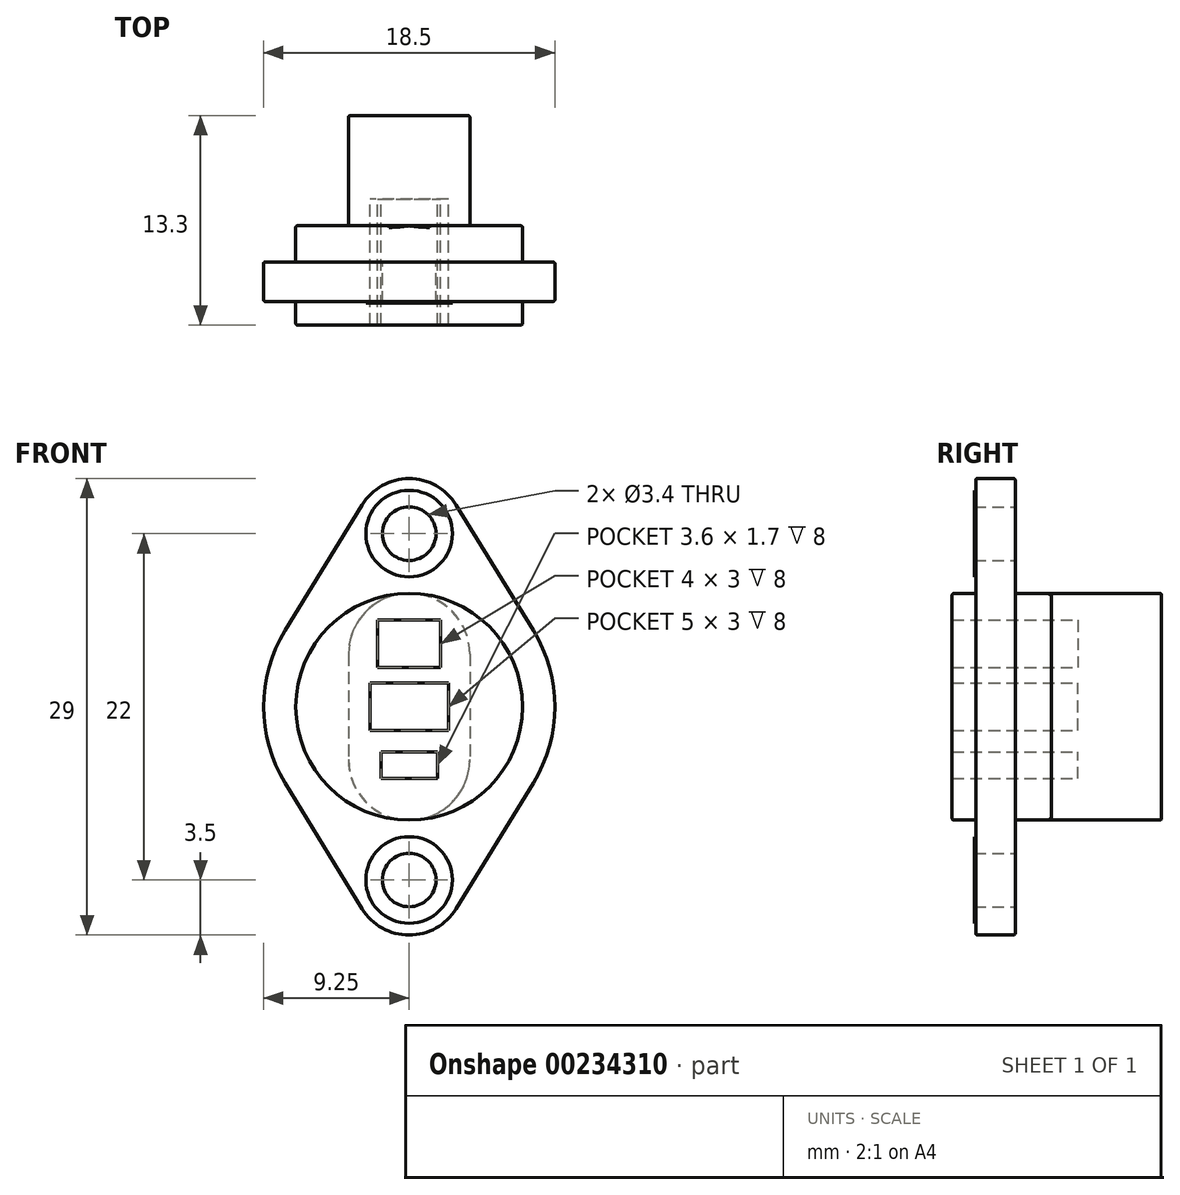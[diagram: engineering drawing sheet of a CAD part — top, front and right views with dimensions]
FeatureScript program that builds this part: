
annotation { "Feature Type Name" : "Feature", "Feature Type Description" : "" }
export const myFeature = defineFeature(function(context is Context, id is Id, definition is map)
    precondition{}
    {
        {
            var Q0;
            Q0=qCreatedBy(makeId("Front.planeOp"),FACE);
            var sketch = newSketch(context, id + "F0", { "sketchPlane" : qUnion([Q0])});
            skCircle(sketch, "E0", {"center": v(0, 11) * mm, "radius": 1.7 * mm});
            skCircle(sketch, "E1", {"center": v(0, -11) * mm, "radius": 1.7 * mm});
            skLineSegment(sketch, "E2", {"start": v(0, 11) * mm, "end": v(0, -11) * mm, "construction": true});
            skPoint(sketch, "E3", {"position": v(0, 0) * mm});
            skCircle(sketch, "E4", {"center": v(0, 0) * mm, "radius": 7.2 * mm});
            skCircle(sketch, "E5", {"center": v(0, -11) * mm, "radius": 2.75 * mm});
            skCircle(sketch, "E6", {"center": v(0, 11) * mm, "radius": 2.75 * mm});
            skCircle(sketch, "E7", {"center": v(0, 11) * mm, "radius": 3.5 * mm});
            skCircle(sketch, "E8", {"center": v(0, -11) * mm, "radius": 3.5 * mm});
            skCircle(sketch, "E9", {"center": v(0, 0) * mm, "radius": 9.25 * mm});
            skLineSegment(sketch, "E10", {"start": v(-2.98, 12.83) * mm, "end": v(-7.89, 4.84) * mm});
            skLineSegment(sketch, "E11", {"start": v(2.98, 12.83) * mm, "end": v(7.89, 4.84) * mm});
            skLineSegment(sketch, "E12", {"start": v(-2.98, -12.83) * mm, "end": v(-7.89, -4.84) * mm});
            skLineSegment(sketch, "E13.bottom", {"start": v(2.5, -1.5) * mm, "end": v(-2.5, -1.5) * mm});
            skLineSegment(sketch, "E13.top", {"start": v(2.5, 1.5) * mm, "end": v(-2.5, 1.5) * mm});
            skLineSegment(sketch, "E13.left", {"start": v(2.5, -1.5) * mm, "end": v(2.5, 1.5) * mm});
            skLineSegment(sketch, "E13.right", {"start": v(-2.5, -1.5) * mm, "end": v(-2.5, 1.5) * mm});
            skLineSegment(sketch, "E14.bottom", {"start": v(-2, 5.5) * mm, "end": v(2, 5.5) * mm});
            skLineSegment(sketch, "E14.top", {"start": v(-2, 2.5) * mm, "end": v(2, 2.5) * mm});
            skLineSegment(sketch, "E14.left", {"start": v(-2, 5.5) * mm, "end": v(-2, 2.5) * mm});
            skLineSegment(sketch, "E14.right", {"start": v(2, 5.5) * mm, "end": v(2, 2.5) * mm});
            skLineSegment(sketch, "E15.bottom", {"start": v(-1.8, -4.56) * mm, "end": v(1.8, -4.56) * mm});
            skLineSegment(sketch, "E15.top", {"start": v(-1.8, -2.86) * mm, "end": v(1.8, -2.86) * mm});
            skLineSegment(sketch, "E15.left", {"start": v(-1.8, -4.56) * mm, "end": v(-1.8, -2.86) * mm});
            skLineSegment(sketch, "E15.right", {"start": v(1.8, -4.56) * mm, "end": v(1.8, -2.86) * mm});
            skPoint(sketch, "E16", {"position": v(0, -2.86) * mm});
            skLineSegment(sketch, "E17", {"start": v(2.98, -12.83) * mm, "end": v(7.89, -4.84) * mm});
            skArc(sketch, "E18", {"start": v(3.85, 3.35) * mm, "mid": v(0, 7.2) * mm, "end": v(-3.85, 3.35) * mm});
            skArc(sketch, "E19", {"start": v(-3.85, -3.35) * mm, "mid": v(0, -7.2) * mm, "end": v(3.85, -3.35) * mm});
            skLineSegment(sketch, "E20", {"start": v(-3.85, 3.35) * mm, "end": v(-3.85, -3.35) * mm});
            skLineSegment(sketch, "E21", {"start": v(3.85, 3.35) * mm, "end": v(3.85, -3.35) * mm});
            skSolve(sketch);
        }
        {
            var Q0;
            Q0=makeQuery(id+"F0.imprint","IMPRINT",FACE,{"disambiguationData":[TD([[makeQuery(id+"F0.imprint","IMPRINT",EDGE,{"derivedFrom":sQuery(id+"F0.wireOp",EDGE,"E4")}),1.0]])]});
            var Q1;
            Q1=makeQuery(id+"F0.imprint","IMPRINT",FACE,{"disambiguationData":[TD([[makeQuery(id+"F0.imprint","IMPRINT",EDGE,{"derivedFrom":sQuery(id+"F0.wireOp",EDGE,"E13.bottom")}),1.0]])]});
            extrude(context, id + "F1", {"entities" : qUnion([Q0, Q1]), "depth" : 1.5 * mm});
        }
        {
            var Q0;
            {var subQ0=sQuery(id+"F0.wireOp",EDGE,"E0");Q0=makeQuery(id+"F0.imprint","IMPRINT",FACE,{"disambiguationData":[TD([[makeQuery(id+"F0.imprint","IMPRINT",EDGE,{"derivedFrom":subQ0}),-1.0]])]});}
            var Q1;
            {var subQ0=sQuery(id+"F0.wireOp",EDGE,"E9");var subQ1=sQuery(id+"F0.wireOp",EDGE,"E6");var subQ2=makeQuery(id+"F0.imprint","INTERSECT",VERTEX,{"disambiguationData":[OD(0.0)],"derivedFrom":[subQ1,subQ0]});Q1=makeQuery(id+"F0.imprint","IMPRINT",FACE,{"disambiguationData":[TD([[makeQuery(id+"F0.imprint","IMPRINT",EDGE,{"disambiguationData":[TD([[subQ2,1.0]])],"derivedFrom":subQ1}),1.0]])]});}
            var Q2;
            {var subQ0=sQuery(id+"F0.wireOp",EDGE,"E1");Q2=makeQuery(id+"F0.imprint","IMPRINT",FACE,{"disambiguationData":[TD([[makeQuery(id+"F0.imprint","IMPRINT",EDGE,{"derivedFrom":subQ0}),-1.0]])]});}
            var Q3;
            {var subQ0=sQuery(id+"F0.wireOp",EDGE,"E9");var subQ1=sQuery(id+"F0.wireOp",EDGE,"E5");var subQ2=makeQuery(id+"F0.imprint","INTERSECT",VERTEX,{"disambiguationData":[OD(0.0)],"derivedFrom":[subQ1,subQ0]});Q3=makeQuery(id+"F0.imprint","IMPRINT",FACE,{"disambiguationData":[TD([[makeQuery(id+"F0.imprint","IMPRINT",EDGE,{"disambiguationData":[TD([[subQ2,1.0]])],"derivedFrom":subQ1}),1.0]])]});}
            extrude(context, id + "F2", {"entities" : qUnion([Q0, Q1, Q2, Q3]), "operationType" : NewBodyOperationType.ADD, "depth" : .1 * mm});
        }
        {
            var Q0;
            {var subQ2=sQuery(id+"F0.wireOp",EDGE,"E9");var subQ6=sQuery(id+"F0.wireOp",EDGE,"E6");var subQ7=makeQuery(id+"F0.imprint","INTERSECT",VERTEX,{"disambiguationData":[OD(0.0)],"derivedFrom":[subQ6,subQ2]});Q0=makeQuery(id+"F0.imprint","IMPRINT",FACE,{"disambiguationData":[TD([[makeQuery(id+"F0.imprint","IMPRINT",EDGE,{"disambiguationData":[TD([[subQ7,-1.0]])],"derivedFrom":subQ6}),-1.0]])]});}
            var Q1;
            {var subQ0=sQuery(id+"F0.wireOp",EDGE,"E0");Q1=makeQuery(id+"F0.imprint","IMPRINT",FACE,{"disambiguationData":[TD([[makeQuery(id+"F0.imprint","IMPRINT",EDGE,{"derivedFrom":subQ0}),-1.0]])]});}
            var Q2;
            {var subQ0=sQuery(id+"F0.wireOp",EDGE,"E10");Q2=makeQuery(id+"F0.imprint","IMPRINT",FACE,{"disambiguationData":[TD([[makeQuery(id+"F0.imprint","IMPRINT",EDGE,{"derivedFrom":subQ0}),1.0]])]});}
            var Q3;
            {var subQ0=sQuery(id+"F0.wireOp",EDGE,"E11");Q3=makeQuery(id+"F0.imprint","IMPRINT",FACE,{"disambiguationData":[TD([[makeQuery(id+"F0.imprint","IMPRINT",EDGE,{"derivedFrom":subQ0}),-1.0]])]});}
            var Q4;
            {var subQ0=sQuery(id+"F0.wireOp",EDGE,"E9");var subQ1=sQuery(id+"F0.wireOp",EDGE,"E6");var subQ2=makeQuery(id+"F0.imprint","INTERSECT",VERTEX,{"disambiguationData":[OD(0.0)],"derivedFrom":[subQ1,subQ0]});Q4=makeQuery(id+"F0.imprint","IMPRINT",FACE,{"disambiguationData":[TD([[makeQuery(id+"F0.imprint","IMPRINT",EDGE,{"disambiguationData":[TD([[subQ2,1.0]])],"derivedFrom":subQ1}),1.0]])]});}
            var Q5;
            {var subQ0=sQuery(id+"F0.wireOp",EDGE,"E9");var subQ1=sQuery(id+"F0.wireOp",EDGE,"E6");var subQ2=makeQuery(id+"F0.imprint","INTERSECT",VERTEX,{"disambiguationData":[OD(0.0)],"derivedFrom":[subQ1,subQ0]});Q5=makeQuery(id+"F0.imprint","IMPRINT",FACE,{"disambiguationData":[TD([[makeQuery(id+"F0.imprint","IMPRINT",EDGE,{"disambiguationData":[TD([[subQ2,1.0]])],"derivedFrom":subQ1}),-1.0]])]});}
            var Q6;
            {var subQ8=sQuery(id+"F0.wireOp",EDGE,"E4");var subQ9=makeQuery(id+"F0.imprint","INTERSECT",VERTEX,{"derivedFrom":[subQ8,sQuery(id+"F0.wireOp",EDGE,"E18")]});Q6=makeQuery(id+"F0.imprint","IMPRINT",FACE,{"disambiguationData":[TD([[makeQuery(id+"F0.imprint","IMPRINT",EDGE,{"disambiguationData":[TD([[subQ9,-1.0]])],"derivedFrom":subQ8}),-1.0]])]});}
            var Q7;
            {var subQ5=sQuery(id+"F0.wireOp",EDGE,"E21");Q7=makeQuery(id+"F0.imprint","IMPRINT",FACE,{"disambiguationData":[TD([[makeQuery(id+"F0.imprint","IMPRINT",EDGE,{"derivedFrom":subQ5}),1.0]])]});}
            var Q8;
            Q8=makeQuery(id+"F0.imprint","IMPRINT",FACE,{"disambiguationData":[TD([[makeQuery(id+"F0.imprint","IMPRINT",EDGE,{"derivedFrom":sQuery(id+"F0.wireOp",EDGE,"E13.bottom")}),1.0]])]});
            var Q9;
            {var subQ5=sQuery(id+"F0.wireOp",EDGE,"E20");Q9=makeQuery(id+"F0.imprint","IMPRINT",FACE,{"disambiguationData":[TD([[makeQuery(id+"F0.imprint","IMPRINT",EDGE,{"derivedFrom":subQ5}),-1.0]])]});}
            var Q10;
            {var subQ0=sQuery(id+"F0.wireOp",EDGE,"E12");Q10=makeQuery(id+"F0.imprint","IMPRINT",FACE,{"disambiguationData":[TD([[makeQuery(id+"F0.imprint","IMPRINT",EDGE,{"derivedFrom":subQ0}),-1.0]])]});}
            var Q11;
            {var subQ0=sQuery(id+"F0.wireOp",EDGE,"E17");Q11=makeQuery(id+"F0.imprint","IMPRINT",FACE,{"disambiguationData":[TD([[makeQuery(id+"F0.imprint","IMPRINT",EDGE,{"derivedFrom":subQ0}),1.0]])]});}
            var Q12;
            {var subQ0=sQuery(id+"F0.wireOp",EDGE,"E9");var subQ1=sQuery(id+"F0.wireOp",EDGE,"E5");var subQ2=makeQuery(id+"F0.imprint","INTERSECT",VERTEX,{"disambiguationData":[OD(0.0)],"derivedFrom":[subQ1,subQ0]});Q12=makeQuery(id+"F0.imprint","IMPRINT",FACE,{"disambiguationData":[TD([[makeQuery(id+"F0.imprint","IMPRINT",EDGE,{"disambiguationData":[TD([[subQ2,1.0]])],"derivedFrom":subQ1}),-1.0]])]});}
            var Q13;
            {var subQ0=sQuery(id+"F0.wireOp",EDGE,"E9");var subQ1=sQuery(id+"F0.wireOp",EDGE,"E5");var subQ2=makeQuery(id+"F0.imprint","INTERSECT",VERTEX,{"disambiguationData":[OD(0.0)],"derivedFrom":[subQ1,subQ0]});Q13=makeQuery(id+"F0.imprint","IMPRINT",FACE,{"disambiguationData":[TD([[makeQuery(id+"F0.imprint","IMPRINT",EDGE,{"disambiguationData":[TD([[subQ2,1.0]])],"derivedFrom":subQ1}),1.0]])]});}
            var Q14;
            {var subQ2=sQuery(id+"F0.wireOp",EDGE,"E9");var subQ6=sQuery(id+"F0.wireOp",EDGE,"E5");var subQ7=makeQuery(id+"F0.imprint","INTERSECT",VERTEX,{"disambiguationData":[OD(0.0)],"derivedFrom":[subQ6,subQ2]});Q14=makeQuery(id+"F0.imprint","IMPRINT",FACE,{"disambiguationData":[TD([[makeQuery(id+"F0.imprint","IMPRINT",EDGE,{"disambiguationData":[TD([[subQ7,-1.0]])],"derivedFrom":subQ6}),-1.0]])]});}
            var Q15;
            {var subQ0=sQuery(id+"F0.wireOp",EDGE,"E1");Q15=makeQuery(id+"F0.imprint","IMPRINT",FACE,{"disambiguationData":[TD([[makeQuery(id+"F0.imprint","IMPRINT",EDGE,{"derivedFrom":subQ0}),-1.0]])]});}
            extrude(context, id + "F3", {"entities" : qUnion([Q0, Q1, Q2, Q3, Q4, Q5, Q6, Q7, Q8, Q9, Q10, Q11, Q12, Q13, Q14, Q15]), "operationType" : NewBodyOperationType.ADD, "oppositeDirection" : true, "depth" : 2.5 * mm});
        }
        {
            var Q0;
            Q0=makeQuery(id+"F0.imprint","IMPRINT",FACE,{"disambiguationData":[TD([[makeQuery(id+"F0.imprint","IMPRINT",EDGE,{"derivedFrom":sQuery(id+"F0.wireOp",EDGE,"E13.bottom")}),1.0]])]});
            var Q1;
            {var subQ5=sQuery(id+"F0.wireOp",EDGE,"E20");Q1=makeQuery(id+"F0.imprint","IMPRINT",FACE,{"disambiguationData":[TD([[makeQuery(id+"F0.imprint","IMPRINT",EDGE,{"derivedFrom":subQ5}),-1.0]])]});}
            var Q2;
            {var subQ5=sQuery(id+"F0.wireOp",EDGE,"E21");Q2=makeQuery(id+"F0.imprint","IMPRINT",FACE,{"disambiguationData":[TD([[makeQuery(id+"F0.imprint","IMPRINT",EDGE,{"derivedFrom":subQ5}),1.0]])]});}
            extrude(context, id + "F4", {"entities" : qUnion([Q0, Q1, Q2]), "operationType" : NewBodyOperationType.ADD, "oppositeDirection" : true, "depth" : 4.8 * mm});
        }
        {
            var Q0;
            Q0=makeQuery(id+"F0.imprint","IMPRINT",FACE,{"disambiguationData":[TD([[makeQuery(id+"F0.imprint","IMPRINT",EDGE,{"derivedFrom":sQuery(id+"F0.wireOp",EDGE,"E13.bottom")}),1.0]])]});
            var Q1;
            Q1=makeQuery(id+"F0.imprint","IMPRINT",FACE,{"disambiguationData":[TD([[makeQuery(id+"F0.imprint","IMPRINT",EDGE,{"derivedFrom":sQuery(id+"F0.wireOp",EDGE,"E14.bottom")}),-1.0]])]});
            var Q2;
            Q2=makeQuery(id+"F0.imprint","IMPRINT",FACE,{"disambiguationData":[TD([[makeQuery(id+"F0.imprint","IMPRINT",EDGE,{"derivedFrom":sQuery(id+"F0.wireOp",EDGE,"E13.bottom")}),-1.0]])]});
            var Q3;
            Q3=makeQuery(id+"F0.imprint","IMPRINT",FACE,{"disambiguationData":[TD([[makeQuery(id+"F0.imprint","IMPRINT",EDGE,{"derivedFrom":sQuery(id+"F0.wireOp",EDGE,"E15.bottom")}),1.0]])]});
            extrude(context, id + "F5", {"entities" : qUnion([Q0, Q1, Q2, Q3]), "operationType" : NewBodyOperationType.ADD, "oppositeDirection" : true, "depth" : 11.8 * mm});
        }
        {
            var Q0;
            Q0=makeQuery(id+"F0.imprint","IMPRINT",FACE,{"disambiguationData":[TD([[makeQuery(id+"F0.imprint","IMPRINT",EDGE,{"derivedFrom":sQuery(id+"F0.wireOp",EDGE,"E14.bottom")}),-1.0]])]});
            var Q1;
            Q1=makeQuery(id+"F0.imprint","IMPRINT",FACE,{"disambiguationData":[TD([[makeQuery(id+"F0.imprint","IMPRINT",EDGE,{"derivedFrom":sQuery(id+"F0.wireOp",EDGE,"E13.bottom")}),-1.0]])]});
            var Q2;
            Q2=makeQuery(id+"F0.imprint","IMPRINT",FACE,{"disambiguationData":[TD([[makeQuery(id+"F0.imprint","IMPRINT",EDGE,{"derivedFrom":sQuery(id+"F0.wireOp",EDGE,"E15.bottom")}),1.0]])]});
            extrude(context, id + "F6", {"entities" : qUnion([Q0, Q1, Q2]), "operationType" : NewBodyOperationType.REMOVE, "oppositeDirection" : true, "depth" : 6.5 * mm});
        }
        {
            var Q0;
            Q0=makeQuery(id+"F1.opExtrude","CAP_EDGE",EDGE,{"disambiguationData":[OSD([sQuery(id+"F0.wireOp",EDGE,"E4")])],"isStart":false});
            var Q1;
            Q1=makeQuery(id+"F3.opExtrude","CAP_EDGE",EDGE,{"disambiguationData":[OSD([sQuery(id+"F0.wireOp",EDGE,"E11")])],"isStart":true});
            var Q2;
            Q2=makeQuery(id+"F3.opExtrude","CAP_EDGE",EDGE,{"disambiguationData":[OSD([sQuery(id+"F0.wireOp",EDGE,"E10")])],"isStart":false});
            var Q3;
            Q3=makeQuery(id+"F5.boolean.opBoolean","SPLIT",EDGE,{"disambiguationData":[OD(0.0)],"derivedFrom":makeQuery(id+"F4.opExtrude","CAP_EDGE",EDGE,{"disambiguationData":[OSD([sQuery(id+"F0.wireOp",EDGE,"E4")])],"isStart":false})});
            var Q4;
            Q4=makeQuery(id+"F5.opExtrude","CAP_EDGE",EDGE,{"disambiguationData":[OSD([sQuery(id+"F0.wireOp",EDGE,"E20")])],"isStart":false});
            fillet(context, id + "F7", {"entities" : qUnion([Q0, Q1, Q2, Q3, Q4]), "radius" : .1 * mm, "tangentPropagation" : true, "allowEdgeOverflow" : false});
        }
    });
